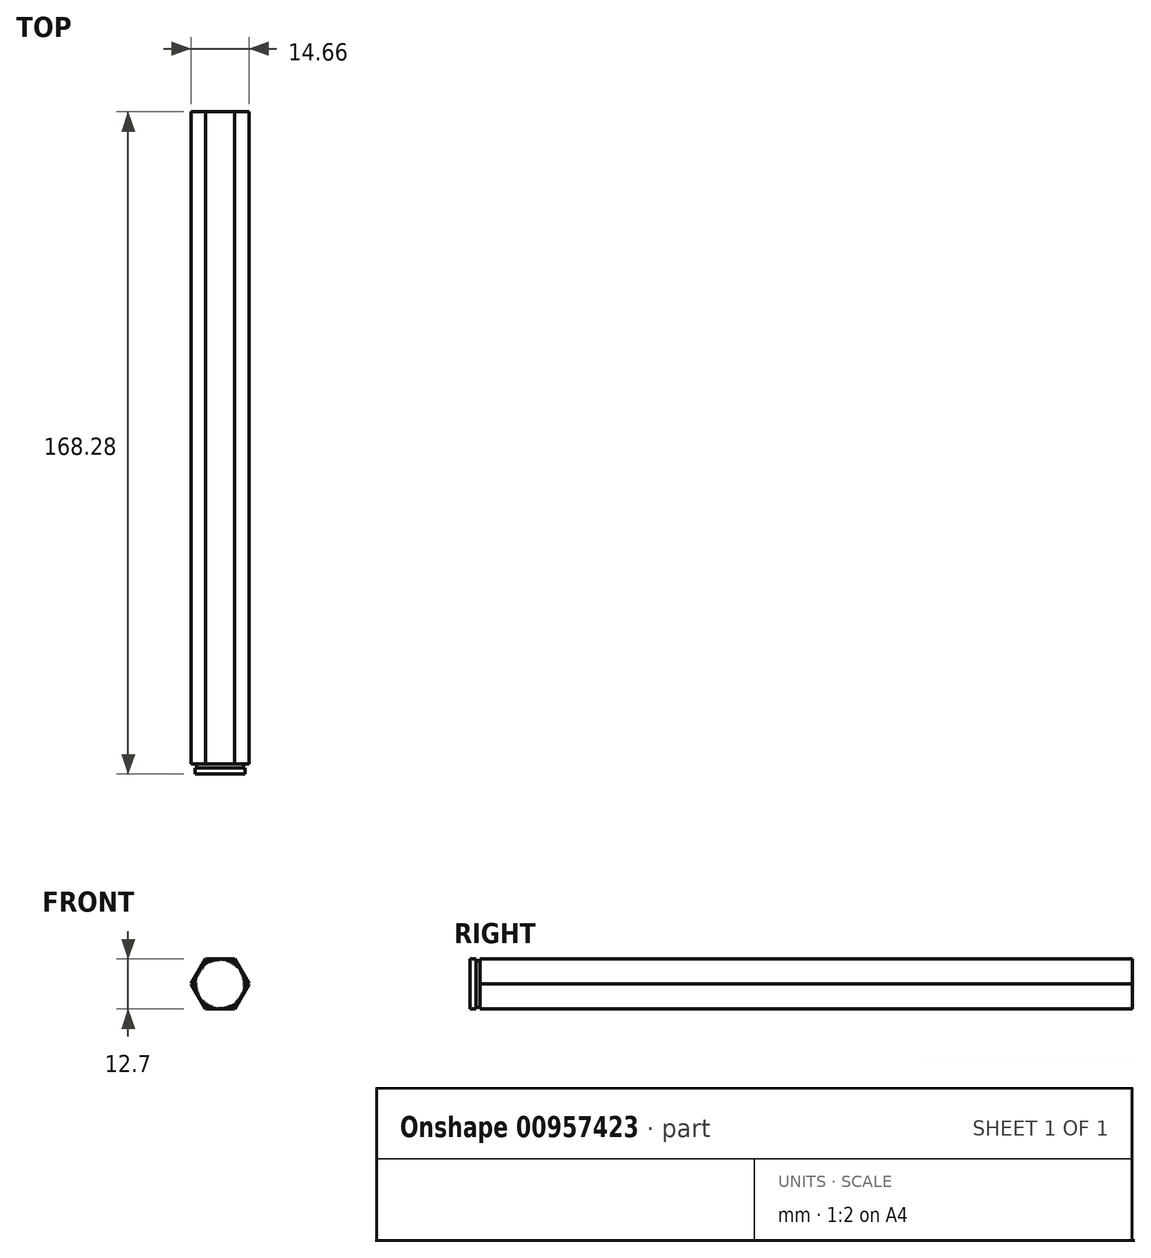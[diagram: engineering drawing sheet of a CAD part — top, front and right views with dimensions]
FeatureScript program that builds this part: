
annotation { "Feature Type Name" : "Feature", "Feature Type Description" : "" }
export const myFeature = defineFeature(function(context is Context, id is Id, definition is map)
    precondition{}
    {
        {
            var Q0;
            Q0=qCreatedBy(makeId("Front.planeOp"),FACE);
            var sketch = newSketch(context, id + "F0", { "sketchPlane" : qUnion([Q0])});
            skCircle(sketch, "E0.cCircle", {"center": v(0, 0) * mm, "radius": 6.35 * mm, "construction": true});
            skLineSegment(sketch, "E0.0", {"start": v(-3.67, 6.35) * mm, "end": v(3.67, 6.35) * mm});
            skLineSegment(sketch, "E0.1", {"start": v(3.67, 6.35) * mm, "end": v(7.33, 0) * mm});
            skLineSegment(sketch, "E0.2", {"start": v(7.33, 0) * mm, "end": v(3.67, -6.35) * mm});
            skLineSegment(sketch, "E0.3", {"start": v(3.67, -6.35) * mm, "end": v(-3.67, -6.35) * mm});
            skLineSegment(sketch, "E0.4", {"start": v(-3.67, -6.35) * mm, "end": v(-7.33, 0) * mm});
            skLineSegment(sketch, "E0.5", {"start": v(-7.33, 0) * mm, "end": v(-3.67, 6.35) * mm});
            skPoint(sketch, "E0.0.midPoint", {"position": v(0, 6.35) * mm});
            skSolve(sketch);
        }
        {
            var Q0;
            Q0 = qSketchRegion(id + "F0", true);
            extrude(context, id + "F1", {"entities" : qUnion([Q0]), "depth" : 168.27 * mm, "offsetDistance" : 25.4 * mm});
        }
        {
            var Q0;
            Q0=qCreatedBy(makeId("Top.planeOp"),FACE);
            var sketch = newSketch(context, id + "F2", { "sketchPlane" : qUnion([Q0])});
            skLineSegment(sketch, "E1", {"start": v(-7.33, -165.7) * mm, "end": v(-5.94, -165.7) * mm});
            skLineSegment(sketch, "E2", {"start": v(-5.94, -165.7) * mm, "end": v(-5.94, -166.69) * mm});
            skLineSegment(sketch, "E3", {"start": v(-5.94, -166.69) * mm, "end": v(-6.35, -166.69) * mm});
            skLineSegment(sketch, "E4", {"start": v(-6.35, -166.69) * mm, "end": v(-6.35, -168.28) * mm});
            skLineSegment(sketch, "E5", {"start": v(0, -168.28) * mm, "end": v(0, 0) * mm, "construction": true});
            skLineSegment(sketch, "E6", {"start": v(-7.33, -165.7) * mm, "end": v(-7.33, -168.28) * mm});
            skLineSegment(sketch, "E7", {"start": v(-7.33, -168.28) * mm, "end": v(-6.35, -168.28) * mm});
            skSolve(sketch);
        }
        {
            var Q0;
            Q0 = qSketchRegion(id + "F2", true);
            var Q1;
            Q1=sQuery(id+"F2.wireOp",EDGE,"E5");
            revolve(context, id + "F3", {"operationType" : NewBodyOperationType.REMOVE, "surfaceOperationType" : NewSurfaceOperationType.NEW, "entities" : qUnion([Q0]), "axis" : qUnion([Q1]), "revolveType" : RevolveType.FULL, "oppositeDirection" : true});
        }
    });
